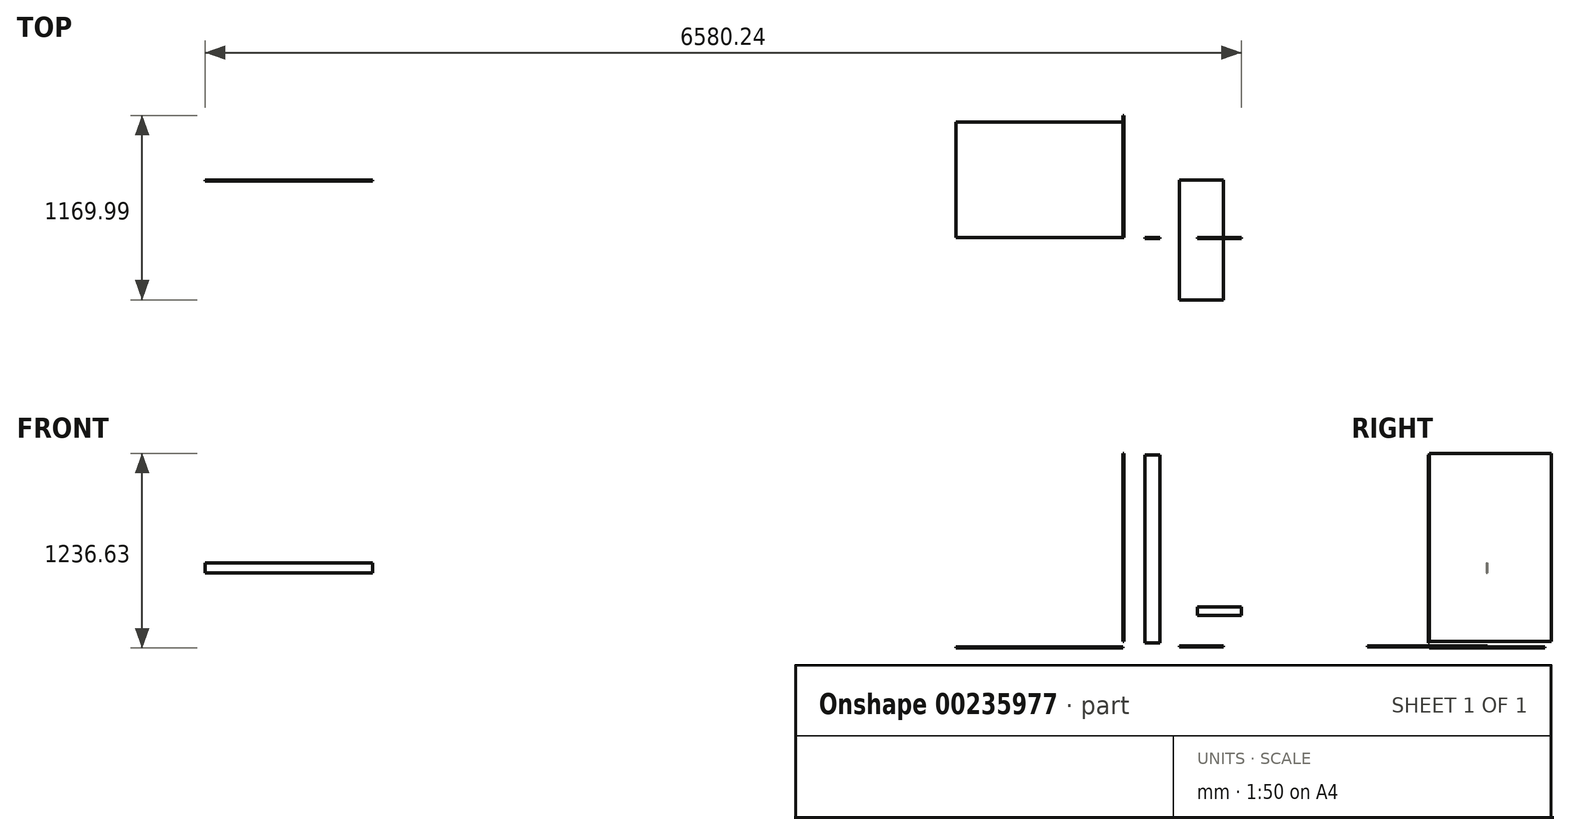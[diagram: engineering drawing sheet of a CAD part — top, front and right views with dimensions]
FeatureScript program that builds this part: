
annotation { "Feature Type Name" : "Feature", "Feature Type Description" : "" }
export const myFeature = defineFeature(function(context is Context, id is Id, definition is map)
    precondition{}
    {
        {
            var Q0;
            Q0=qCreatedBy(makeId("Top.planeOp"),FACE);
            var sketch = newSketch(context, id + "F0", { "sketchPlane" : qUnion([Q0])});
            skLineSegment(sketch, "E0.bottom", {"start": v(531.81, -366.71) * mm, "end": v(-531.81, -366.71) * mm});
            skLineSegment(sketch, "E0.top", {"start": v(531.81, 366.71) * mm, "end": v(-531.81, 366.71) * mm});
            skLineSegment(sketch, "E0.left", {"start": v(531.81, -366.71) * mm, "end": v(531.81, 366.71) * mm});
            skLineSegment(sketch, "E0.right", {"start": v(-531.81, -366.71) * mm, "end": v(-531.81, 366.71) * mm});
            skPoint(sketch, "E0.middle", {"position": v(0, 0) * mm});
            skSolve(sketch);
        }
        {
            var Q0;
            Q0 = qSketchRegion(id + "F0", true);
            extrude(context, id + "F1", {"entities" : qUnion([Q0]), "depth" : 6.35 * mm});
        }
        {
            var Q0;
            Q0=makeQuery(id+"F1.opExtrude","SWEPT_FACE",FACE,{"disambiguationData":[OSD([sQuery(id+"F0.wireOp",EDGE,"E0.left")])]});
            var sketch = newSketch(context, id + "F2", { "sketchPlane" : qUnion([Q0])});
            skLineSegment(sketch, "E1.bottom", {"start": v(-366.71, 42.83) * mm, "end": v(407.99, 42.83) * mm});
            skLineSegment(sketch, "E1.top", {"start": v(-366.71, 1236.63) * mm, "end": v(407.99, 1236.63) * mm});
            skLineSegment(sketch, "E1.left", {"start": v(-366.71, 42.83) * mm, "end": v(-366.71, 1236.63) * mm});
            skLineSegment(sketch, "E1.right", {"start": v(407.99, 42.83) * mm, "end": v(407.99, 1236.63) * mm});
            skSolve(sketch);
        }
        {
            var Q0;
            Q0 = qSketchRegion(id + "F2", true);
            extrude(context, id + "F3", {"entities" : qUnion([Q0]), "depth" : 6.35 * mm});
        }
        {
            var Q0;
            Q0=makeQuery(id+"F1.opExtrude","SWEPT_FACE",FACE,{"disambiguationData":[OSD([sQuery(id+"F0.wireOp",EDGE,"E0.bottom")])]});
            var sketch = newSketch(context, id + "F4", { "sketchPlane" : qUnion([Q0])});
            skLineSegment(sketch, "E2.bottom", {"start": v(668.97, 33.04) * mm, "end": v(764.22, 33.04) * mm});
            skLineSegment(sketch, "E2.top", {"start": v(668.97, 1226.84) * mm, "end": v(764.22, 1226.84) * mm});
            skLineSegment(sketch, "E2.left", {"start": v(668.97, 33.04) * mm, "end": v(668.97, 1226.84) * mm});
            skLineSegment(sketch, "E2.right", {"start": v(764.22, 33.04) * mm, "end": v(764.22, 1226.84) * mm});
            skSolve(sketch);
        }
        {
            var Q0;
            Q0 = qSketchRegion(id + "F4", true);
            extrude(context, id + "F5", {"entities" : qUnion([Q0]), "depth" : 6.35 * mm});
        }
        {
            var Q0;
            Q0=makeQuery(id+"F1.opExtrude","CAP_FACE",FACE,{"disambiguationData":[OSD([sQuery(id+"F0.wireOp",EDGE,"E0.bottom"),sQuery(id+"F0.wireOp",EDGE,"E0.top"),sQuery(id+"F0.wireOp",EDGE,"E0.left"),sQuery(id+"F0.wireOp",EDGE,"E0.right")])],"isStart":false});
            var sketch = newSketch(context, id + "F6", { "sketchPlane" : qUnion([Q0])});
            skLineSegment(sketch, "E3.bottom", {"start": v(888.6, -762) * mm, "end": v(1168, -762) * mm});
            skLineSegment(sketch, "E3.top", {"start": v(888.6, 0) * mm, "end": v(1168, 0) * mm});
            skLineSegment(sketch, "E3.left", {"start": v(888.6, -762) * mm, "end": v(888.6, 0) * mm});
            skLineSegment(sketch, "E3.right", {"start": v(1168, -762) * mm, "end": v(1168, 0) * mm});
            skSolve(sketch);
        }
        {
            var Q0;
            Q0 = qSketchRegion(id + "F6", true);
            extrude(context, id + "F7", {"entities" : qUnion([Q0]), "depth" : 6.35 * mm});
        }
        {
            var Q0;
            Q0=makeQuery(id+"F1.opExtrude","SWEPT_FACE",FACE,{"disambiguationData":[OSD([sQuery(id+"F0.wireOp",EDGE,"E0.bottom")])]});
            var sketch = newSketch(context, id + "F8", { "sketchPlane" : qUnion([Q0])});
            skLineSegment(sketch, "E4.bottom", {"start": v(1002.4, 261.65) * mm, "end": v(1281.8, 261.65) * mm});
            skLineSegment(sketch, "E4.top", {"start": v(1002.4, 207.67) * mm, "end": v(1281.8, 207.67) * mm});
            skLineSegment(sketch, "E4.left", {"start": v(1002.4, 261.65) * mm, "end": v(1002.4, 207.67) * mm});
            skLineSegment(sketch, "E4.right", {"start": v(1281.8, 261.65) * mm, "end": v(1281.8, 207.67) * mm});
            skSolve(sketch);
        }
        {
            var Q0;
            Q0 = qSketchRegion(id + "F8", true);
            extrude(context, id + "F9", {"entities" : qUnion([Q0]), "depth" : 6.35 * mm});
        }
        {
            var Q0;
            Q0=qCreatedBy(makeId("Front.planeOp"),FACE);
            var sketch = newSketch(context, id + "F10", { "sketchPlane" : qUnion([Q0])});
            skLineSegment(sketch, "E5.bottom", {"start": v(-5298.45, 540.76) * mm, "end": v(-4234.82, 540.76) * mm});
            skLineSegment(sketch, "E5.top", {"start": v(-5298.45, 477.26) * mm, "end": v(-4234.82, 477.26) * mm});
            skLineSegment(sketch, "E5.left", {"start": v(-5298.45, 540.76) * mm, "end": v(-5298.45, 477.26) * mm});
            skLineSegment(sketch, "E5.right", {"start": v(-4234.82, 540.76) * mm, "end": v(-4234.82, 477.26) * mm});
            skSolve(sketch);
        }
        {
            var Q0;
            Q0 = qSketchRegion(id + "F10", true);
            extrude(context, id + "F11", {"entities" : qUnion([Q0]), "depth" : 6.35 * mm});
        }
    });
